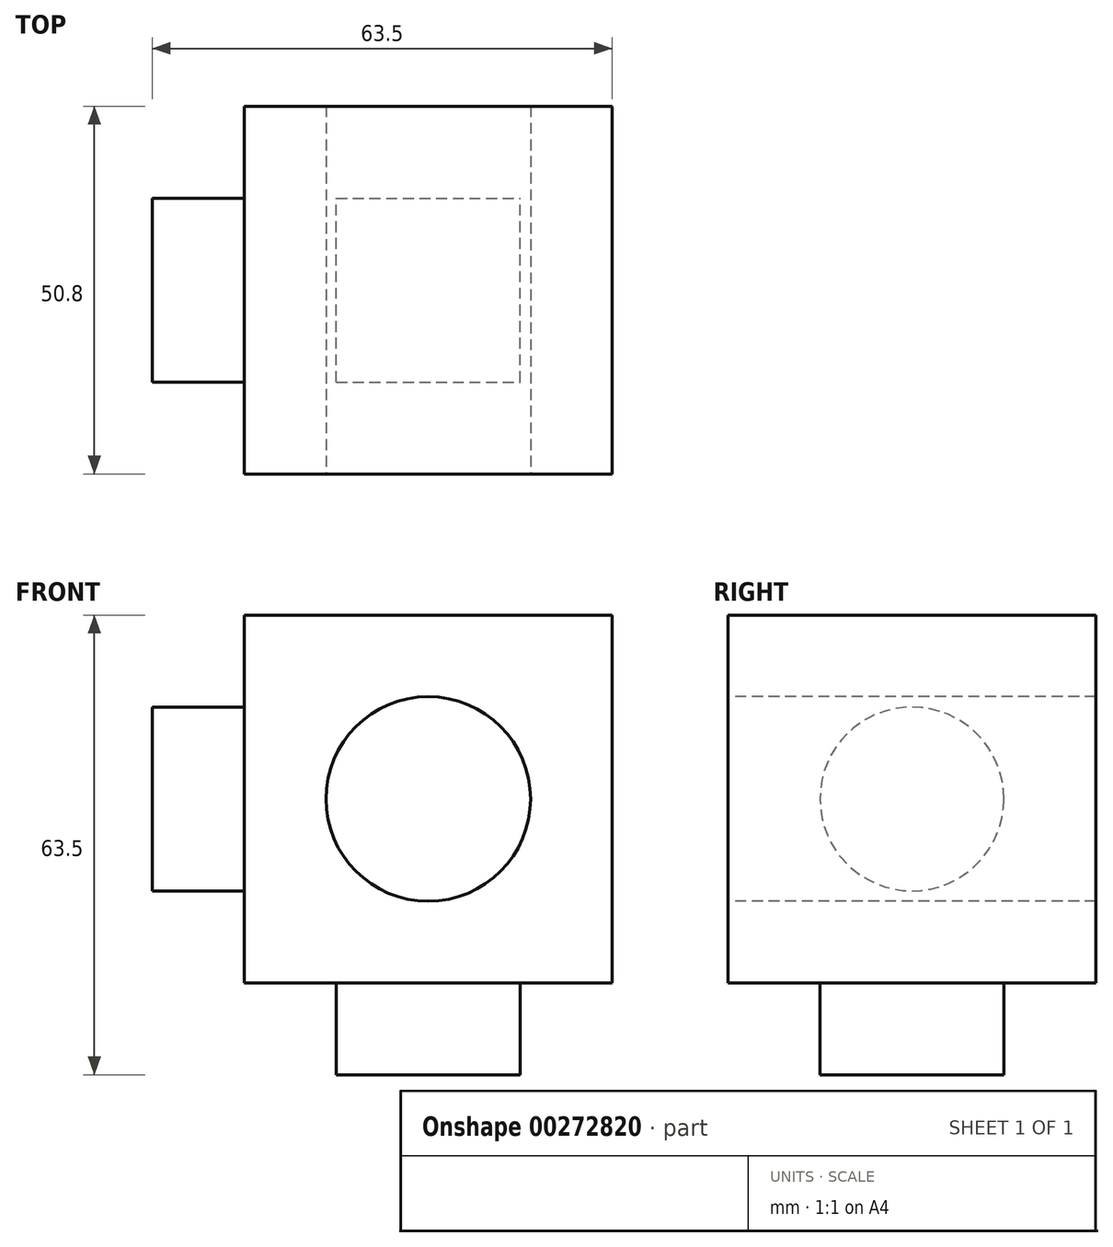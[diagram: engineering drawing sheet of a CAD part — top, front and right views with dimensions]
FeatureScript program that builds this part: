
annotation { "Feature Type Name" : "Feature", "Feature Type Description" : "" }
export const myFeature = defineFeature(function(context is Context, id is Id, definition is map)
    precondition{}
    {
        {
            var Q0;
            Q0=qCreatedBy(makeId("Front.planeOp"),FACE);
            var sketch = newSketch(context, id + "F0", { "sketchPlane" : qUnion([Q0])});
            skLineSegment(sketch, "E0.bottom", {"start": v(0, 0) * mm, "end": v(-50.8, 0) * mm});
            skLineSegment(sketch, "E0.top", {"start": v(0, 50.8) * mm, "end": v(-50.8, 50.8) * mm});
            skLineSegment(sketch, "E0.left", {"start": v(0, 0) * mm, "end": v(0, 50.8) * mm});
            skLineSegment(sketch, "E0.right", {"start": v(-50.8, 0) * mm, "end": v(-50.8, 50.8) * mm});
            skSolve(sketch);
        }
        {
            var Q0;
            Q0 = qSketchRegion(id + "F0", true);
            extrude(context, id + "F1", {"entities" : qUnion([Q0]), "depth" : 50.8 * mm});
        }
        {
            var Q0;
            Q0=makeQuery(id+"F1.opExtrude","CAP_FACE",FACE,{"disambiguationData":[OSD([sQuery(id+"F0.wireOp",EDGE,"E0.bottom"),sQuery(id+"F0.wireOp",EDGE,"E0.top"),sQuery(id+"F0.wireOp",EDGE,"E0.left"),sQuery(id+"F0.wireOp",EDGE,"E0.right")])],"isStart":false});
            var sketch = newSketch(context, id + "F2", { "sketchPlane" : qUnion([Q0])});
            skCircle(sketch, "E1", {"center": v(-25.4, 25.4) * mm, "radius": 14.13 * mm});
            skSolve(sketch);
        }
        {
            var Q0;
            Q0=makeQuery(id+"F2.imprint","IMPRINT",FACE,{"disambiguationData":[TD([[makeQuery(id+"F2.imprint","IMPRINT",EDGE,{"derivedFrom":sQuery(id+"F2.wireOp",EDGE,"E1")}),1.0]])]});
            extrude(context, id + "F3", {"entities" : qUnion([Q0]), "operationType" : NewBodyOperationType.REMOVE, "oppositeDirection" : true, "depth" : 50.8 * mm});
        }
        {
            var Q0;
            Q0=makeQuery(id+"F1.opExtrude","SWEPT_FACE",FACE,{"disambiguationData":[OSD([sQuery(id+"F0.wireOp",EDGE,"E0.bottom")])]});
            var sketch = newSketch(context, id + "F4", { "sketchPlane" : qUnion([Q0])});
            skLineSegment(sketch, "E2.bottom", {"start": v(-38.1, 38.1) * mm, "end": v(-12.7, 38.1) * mm});
            skLineSegment(sketch, "E2.top", {"start": v(-38.1, 12.7) * mm, "end": v(-12.7, 12.7) * mm});
            skLineSegment(sketch, "E2.left", {"start": v(-38.1, 38.1) * mm, "end": v(-38.1, 12.7) * mm});
            skLineSegment(sketch, "E2.right", {"start": v(-12.7, 38.1) * mm, "end": v(-12.7, 12.7) * mm});
            skSolve(sketch);
        }
        {
            var Q0;
            Q0=makeQuery(id+"F4.imprint","IMPRINT",FACE,{"disambiguationData":[TD([[makeQuery(id+"F4.imprint","IMPRINT",EDGE,{"derivedFrom":sQuery(id+"F4.wireOp",EDGE,"E2.bottom")}),-1.0]])]});
            extrude(context, id + "F5", {"entities" : qUnion([Q0]), "operationType" : NewBodyOperationType.ADD, "depth" : 12.7 * mm});
        }
        {
            var Q0;
            Q0=makeQuery(id+"F1.opExtrude","SWEPT_FACE",FACE,{"disambiguationData":[OSD([sQuery(id+"F0.wireOp",EDGE,"E0.right")])]});
            var sketch = newSketch(context, id + "F6", { "sketchPlane" : qUnion([Q0])});
            skCircle(sketch, "E3", {"center": v(25.4, 25.4) * mm, "radius": 12.7 * mm});
            skSolve(sketch);
        }
        {
            var Q0;
            Q0=makeQuery(id+"F6.imprint","IMPRINT",FACE,{"disambiguationData":[TD([[makeQuery(id+"F6.imprint","IMPRINT",EDGE,{"derivedFrom":sQuery(id+"F6.wireOp",EDGE,"E3")}),1.0]])]});
            extrude(context, id + "F7", {"entities" : qUnion([Q0]), "operationType" : NewBodyOperationType.ADD, "depth" : 12.7 * mm});
        }
    });
